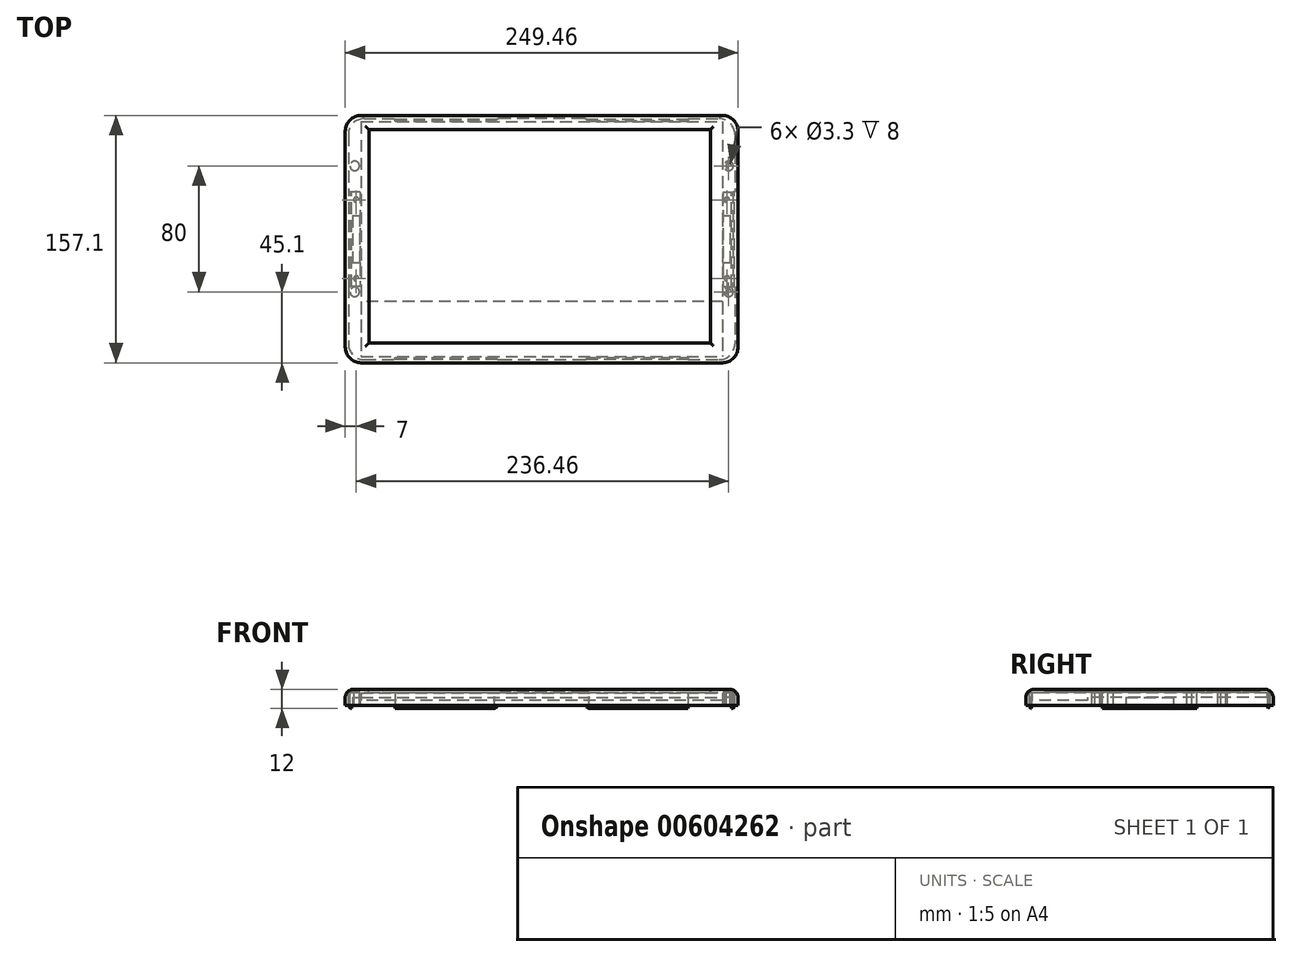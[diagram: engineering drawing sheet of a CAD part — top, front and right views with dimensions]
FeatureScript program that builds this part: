
annotation { "Feature Type Name" : "Feature", "Feature Type Description" : "" }
export const myFeature = defineFeature(function(context is Context, id is Id, definition is map)
    precondition{}
    {
        {
            var Q0;
            Q0=qCreatedBy(makeId("Top.planeOp"),FACE);
            var sketch = newSketch(context, id + "F0", { "sketchPlane" : qUnion([Q0])});
            skLineSegment(sketch, "E0.bottom", {"start": v(-114.73, 74.55) * mm, "end": v(114.73, 74.55) * mm});
            skLineSegment(sketch, "E0.top", {"start": v(-114.73, -74.55) * mm, "end": v(114.73, -74.55) * mm});
            skLineSegment(sketch, "E0.left", {"start": v(-114.73, 74.55) * mm, "end": v(-114.73, -74.55) * mm});
            skLineSegment(sketch, "E0.right", {"start": v(114.73, 74.55) * mm, "end": v(114.73, -74.55) * mm});
            skPoint(sketch, "E0.middle", {"position": v(0, 0) * mm});
            skLineSegment(sketch, "E1.bottom", {"start": v(-111.27, 71.12) * mm, "end": v(108.7, 71.12) * mm});
            skLineSegment(sketch, "E1.top", {"start": v(-111.27, -67.78) * mm, "end": v(108.7, -67.78) * mm});
            skLineSegment(sketch, "E1.left", {"start": v(-111.27, 71.12) * mm, "end": v(-111.27, -67.78) * mm});
            skLineSegment(sketch, "E1.right", {"start": v(108.7, 71.12) * mm, "end": v(108.7, -67.78) * mm});
            skLineSegment(sketch, "E2.bottom", {"start": v(-109.77, 69.62) * mm, "end": v(107.2, 69.62) * mm});
            skLineSegment(sketch, "E2.top", {"start": v(-109.77, -65.98) * mm, "end": v(107.2, -65.98) * mm});
            skLineSegment(sketch, "E2.left", {"start": v(-109.77, 69.62) * mm, "end": v(-109.77, -65.98) * mm});
            skLineSegment(sketch, "E2.right", {"start": v(107.2, 69.62) * mm, "end": v(107.2, -65.98) * mm});
            skLineSegment(sketch, "E3.bottom", {"start": v(-122.73, 76.55) * mm, "end": v(122.73, 76.55) * mm});
            skLineSegment(sketch, "E3.top", {"start": v(-122.73, -76.55) * mm, "end": v(122.73, -76.55) * mm});
            skLineSegment(sketch, "E3.left", {"start": v(-122.73, 76.55) * mm, "end": v(-122.73, -76.55) * mm});
            skLineSegment(sketch, "E3.right", {"start": v(122.73, 76.55) * mm, "end": v(122.73, -76.55) * mm});
            skLineSegment(sketch, "E4.0", {"start": v(-124.73, 78.55) * mm, "end": v(124.73, 78.55) * mm});
            skLineSegment(sketch, "E4.1", {"start": v(-124.73, 78.55) * mm, "end": v(-124.73, -78.55) * mm});
            skLineSegment(sketch, "E4.2", {"start": v(-124.73, -78.55) * mm, "end": v(124.73, -78.55) * mm});
            skLineSegment(sketch, "E4.3", {"start": v(124.73, 78.55) * mm, "end": v(124.73, -78.55) * mm});
            skSolve(sketch);
        }
        {
            var Q0;
            Q0=makeQuery(id+"F0.imprint","IMPRINT",FACE,{"disambiguationData":[TD([[makeQuery(id+"F0.imprint","IMPRINT",EDGE,{"derivedFrom":sQuery(id+"F0.wireOp",EDGE,"E0.bottom")}),-1.0]])]});
            var Q1;
            Q1=makeQuery(id+"F0.imprint","IMPRINT",FACE,{"disambiguationData":[TD([[makeQuery(id+"F0.imprint","IMPRINT",EDGE,{"derivedFrom":sQuery(id+"F0.wireOp",EDGE,"E1.bottom")}),-1.0]])]});
            var Q2;
            Q2=makeQuery(id+"F0.imprint","IMPRINT",FACE,{"disambiguationData":[TD([[makeQuery(id+"F0.imprint","IMPRINT",EDGE,{"derivedFrom":sQuery(id+"F0.wireOp",EDGE,"E0.bottom")}),1.0]])]});
            extrude(context, id + "F1", {"entities" : qUnion([Q0, Q1, Q2]), "depth" : 2 * mm, "offsetDistance" : 25 * mm});
        }
        {
            var Q0;
            Q0=makeQuery(id+"F1.opExtrude","CAP_EDGE",EDGE,{"disambiguationData":[OSD([sQuery(id+"F0.wireOp",EDGE,"E2.left")])],"isStart":false});
            var Q1;
            Q1=makeQuery(id+"F1.opExtrude","CAP_EDGE",EDGE,{"disambiguationData":[OSD([sQuery(id+"F0.wireOp",EDGE,"E2.top")])],"isStart":false});
            var Q2;
            Q2=makeQuery(id+"F1.opExtrude","CAP_EDGE",EDGE,{"disambiguationData":[OSD([sQuery(id+"F0.wireOp",EDGE,"E2.right")])],"isStart":false});
            var Q3;
            Q3=makeQuery(id+"F1.opExtrude","CAP_EDGE",EDGE,{"disambiguationData":[OSD([sQuery(id+"F0.wireOp",EDGE,"E2.bottom")])],"isStart":false});
            fillet(context, id + "F2", {"entities" : qUnion([Q0, Q1, Q2, Q3]), "radius" : 2 * mm, "tangentPropagation" : true, "allowEdgeOverflow" : false});
        }
        {
            var Q0;
            Q0=makeQuery(id+"F0.imprint","IMPRINT",FACE,{"disambiguationData":[TD([[makeQuery(id+"F0.imprint","IMPRINT",EDGE,{"derivedFrom":sQuery(id+"F0.wireOp",EDGE,"E2.bottom")}),-1.0]])]});
            var Q1;
            Q1=makeQuery(id+"F0.imprint","IMPRINT",FACE,{"disambiguationData":[TD([[makeQuery(id+"F0.imprint","IMPRINT",EDGE,{"derivedFrom":sQuery(id+"F0.wireOp",EDGE,"E0.bottom")}),-1.0]])]});
            var Q2;
            Q2=makeQuery(id+"F0.imprint","IMPRINT",FACE,{"disambiguationData":[TD([[makeQuery(id+"F0.imprint","IMPRINT",EDGE,{"derivedFrom":sQuery(id+"F0.wireOp",EDGE,"E1.bottom")}),-1.0]])]});
            extrude(context, id + "F3", {"entities" : qUnion([Q0, Q1, Q2]), "depth" : 4.7 * mm, "offsetDistance" : 25 * mm});
        }
        {
            var Q0;
            Q0=makeQuery(id+"F3.opExtrude","SWEPT_BODY",BODY,{"disambiguationData":[OSD([sQuery(id+"F0.wireOp",EDGE,"E0.bottom"),sQuery(id+"F0.wireOp",EDGE,"E0.top"),sQuery(id+"F0.wireOp",EDGE,"E0.left"),sQuery(id+"F0.wireOp",EDGE,"E0.right")])]});
            transform(context, id + "F4", {"entities" : qUnion([Q0]), "transformType" : TransformType.TRANSLATION_3D, "dx" : 0 * mm, "dy" : 0 * mm, "dz" : -4.8 * mm, "makeCopy" : false});
        }
        {
            var Q0;
            Q0=makeQuery(id+"F3.opExtrude","CAP_FACE",FACE,{"disambiguationData":[OSD([sQuery(id+"F0.wireOp",EDGE,"E0.bottom"),sQuery(id+"F0.wireOp",EDGE,"E0.top"),sQuery(id+"F0.wireOp",EDGE,"E0.left"),sQuery(id+"F0.wireOp",EDGE,"E0.right")])],"isStart":true});
            var sketch = newSketch(context, id + "F5", { "sketchPlane" : qUnion([Q0])});
            skLineSegment(sketch, "E5", {"start": v(114.73, 39.55) * mm, "end": v(-114.73, 39.55) * mm});
            skSolve(sketch);
        }
        {
            var Q0;
            Q0=qSketchRegion(id+"F5",true);
            var Q1;
            {var subQ0=sQuery(id+"F5.wireOp",EDGE,"E5");Q1=makeQuery(id+"F5.imprint","IMPRINT",FACE,{"disambiguationData":[TD([[makeQuery(id+"F5.imprint","IMPRINT",EDGE,{"derivedFrom":subQ0}),1.0]])]});}
            extrude(context, id + "F6", {"entities" : qUnion([Q0, Q1]), "operationType" : NewBodyOperationType.REMOVE, "oppositeDirection" : true, "depth" : 1.75 * mm, "offsetDistance" : 25 * mm});
        }
        {
            var Q0;
            Q0=makeQuery(id+"F1.opExtrude","CAP_FACE",FACE,{"disambiguationData":[OSD([sQuery(id+"F0.wireOp",EDGE,"E2.bottom"),sQuery(id+"F0.wireOp",EDGE,"E2.top"),sQuery(id+"F0.wireOp",EDGE,"E2.left"),sQuery(id+"F0.wireOp",EDGE,"E2.right"),sQuery(id+"F0.wireOp",EDGE,"E3.bottom"),sQuery(id+"F0.wireOp",EDGE,"E3.top"),sQuery(id+"F0.wireOp",EDGE,"E3.left"),sQuery(id+"F0.wireOp",EDGE,"E3.right")])],"isStart":true});
            var sketch = newSketch(context, id + "F7", { "sketchPlane" : qUnion([Q0])});
            skCircle(sketch, "E6", {"center": v(118.73, -46.55) * mm, "radius": 3 * mm});
            skCircle(sketch, "E7", {"center": v(118.73, 33.45) * mm, "radius": 3 * mm});
            skCircle(sketch, "E8.MirrorC", {"center": v(-118.73, -46.55) * mm, "radius": 3 * mm});
            skCircle(sketch, "E9.MirrorC", {"center": v(-118.73, 33.45) * mm, "radius": 3 * mm});
            skSolve(sketch);
        }
        {
            var Q0;
            Q0=qSketchRegion(id+"F7",true);
            extrude(context, id + "F8", {"entities" : qUnion([Q0]), "operationType" : NewBodyOperationType.ADD, "depth" : 8 * mm, "offsetDistance" : 25 * mm});
        }
        {
            var Q0;
            Q0=makeQuery(id+"F0.imprint","IMPRINT",FACE,{"disambiguationData":[TD([[makeQuery(id+"F0.imprint","IMPRINT",EDGE,{"derivedFrom":sQuery(id+"F0.wireOp",EDGE,"E3.bottom")}),1.0]])]});
            var Q1;
            Q1=makeQuery(id+"F1.opExtrude","CAP_FACE",FACE,{"disambiguationData":[OSD([sQuery(id+"F0.wireOp",EDGE,"E2.bottom"),sQuery(id+"F0.wireOp",EDGE,"E2.top"),sQuery(id+"F0.wireOp",EDGE,"E2.left"),sQuery(id+"F0.wireOp",EDGE,"E2.right"),sQuery(id+"F0.wireOp",EDGE,"E3.bottom"),sQuery(id+"F0.wireOp",EDGE,"E3.top"),sQuery(id+"F0.wireOp",EDGE,"E3.left"),sQuery(id+"F0.wireOp",EDGE,"E3.right")])],"isStart":false});
            extrude(context, id + "F9", {"entities" : qUnion([Q0]), "operationType" : NewBodyOperationType.ADD, "endBound" : BoundingType.UP_TO_SURFACE, "depth" : 25 * mm, "endBoundEntityFace" : qUnion([Q1]), "offsetDistance" : 25 * mm});
        }
        {
            var Q0;
            Q0=makeQuery(id+"F0.imprint","IMPRINT",FACE,{"disambiguationData":[TD([[makeQuery(id+"F0.imprint","IMPRINT",EDGE,{"derivedFrom":sQuery(id+"F0.wireOp",EDGE,"E3.bottom")}),1.0]])]});
            extrude(context, id + "F10", {"entities" : qUnion([Q0]), "operationType" : NewBodyOperationType.ADD, "oppositeDirection" : true, "depth" : 8 * mm, "offsetDistance" : 25 * mm});
        }
        {
            var Q0;
            Q0=makeQuery(id+"F10.opExtrude","SWEPT_FACE",FACE,{"disambiguationData":[OSD([sQuery(id+"F0.wireOp",EDGE,"E3.top")])]});
            var sketch = newSketch(context, id + "F11", { "sketchPlane" : qUnion([Q0])});
            skLineSegment(sketch, "E10.bottom", {"start": v(-93, 0) * mm, "end": v(-85, 0) * mm});
            skLineSegment(sketch, "E10.top", {"start": v(-93, -8) * mm, "end": v(-85, -8) * mm});
            skLineSegment(sketch, "E10.left", {"start": v(-93, 0) * mm, "end": v(-93, -8) * mm});
            skLineSegment(sketch, "E10.right", {"start": v(-85, 0) * mm, "end": v(-85, -8) * mm});
            skLineSegment(sketch, "E11.MirrorCS", {"start": v(93, 0) * mm, "end": v(93, -8) * mm});
            skLineSegment(sketch, "E12.MirrorCS", {"start": v(93, 0) * mm, "end": v(85, 0) * mm});
            skLineSegment(sketch, "E13.MirrorCS", {"start": v(85, 0) * mm, "end": v(85, -8) * mm});
            skLineSegment(sketch, "E14.MirrorCS", {"start": v(93, -8) * mm, "end": v(85, -8) * mm});
            skSolve(sketch);
        }
        {
            var Q0;
            Q0=makeQuery(id+"F11.imprint","IMPRINT",FACE,{"disambiguationData":[TD([[makeQuery(id+"F11.imprint","IMPRINT",EDGE,{"derivedFrom":sQuery(id+"F11.wireOp",EDGE,"E10.bottom")}),1.0]])]});
            var Q1;
            Q1=makeQuery(id+"F11.imprint","IMPRINT",FACE,{"disambiguationData":[TD([[makeQuery(id+"F11.imprint","IMPRINT",EDGE,{"derivedFrom":sQuery(id+"F11.wireOp",EDGE,"E11.MirrorCS")}),-1.0]])]});
            extrude(context, id + "F12", {"entities" : qUnion([Q0, Q1]), "operationType" : NewBodyOperationType.ADD, "depth" : 1.7 * mm, "offsetDistance" : 25 * mm});
        }
        {
            var Q0;
            Q0=makeQuery(id+"F10.opExtrude","SWEPT_FACE",FACE,{"disambiguationData":[OSD([sQuery(id+"F0.wireOp",EDGE,"E3.bottom")])]});
            var sketch = newSketch(context, id + "F13", { "sketchPlane" : qUnion([Q0])});
            skLineSegment(sketch, "E15.bottom", {"start": v(-93, 0) * mm, "end": v(-85, 0) * mm});
            skLineSegment(sketch, "E15.top", {"start": v(-93, -8) * mm, "end": v(-85, -8) * mm});
            skLineSegment(sketch, "E15.left", {"start": v(-93, 0) * mm, "end": v(-93, -8) * mm});
            skLineSegment(sketch, "E15.right", {"start": v(-85, 0) * mm, "end": v(-85, -8) * mm});
            skLineSegment(sketch, "E16.MirrorCS", {"start": v(93, 0) * mm, "end": v(93, -8) * mm});
            skLineSegment(sketch, "E17.MirrorCS", {"start": v(85, 0) * mm, "end": v(85, -8) * mm});
            skLineSegment(sketch, "E18.MirrorCS", {"start": v(93, 0) * mm, "end": v(85, 0) * mm});
            skLineSegment(sketch, "E19.MirrorCS", {"start": v(93, -8) * mm, "end": v(85, -8) * mm});
            skSolve(sketch);
        }
        {
            var Q0;
            Q0=makeQuery(id+"F13.imprint","IMPRINT",FACE,{"disambiguationData":[TD([[makeQuery(id+"F13.imprint","IMPRINT",EDGE,{"derivedFrom":sQuery(id+"F13.wireOp",EDGE,"E15.bottom")}),-1.0]])]});
            var Q1;
            Q1=makeQuery(id+"F13.imprint","IMPRINT",FACE,{"disambiguationData":[TD([[makeQuery(id+"F13.imprint","IMPRINT",EDGE,{"derivedFrom":sQuery(id+"F13.wireOp",EDGE,"E16.MirrorCS")}),-1.0]])]});
            extrude(context, id + "F14", {"entities" : qUnion([Q0, Q1]), "operationType" : NewBodyOperationType.ADD, "depth" : 1.7 * mm, "offsetDistance" : 25 * mm});
        }
        {
            var Q0;
            Q0=makeQuery(id+"F10.opExtrude","SWEPT_FACE",FACE,{"disambiguationData":[OSD([sQuery(id+"F0.wireOp",EDGE,"E3.left")])]});
            var sketch = newSketch(context, id + "F15", { "sketchPlane" : qUnion([Q0])});
            skLineSegment(sketch, "E20.bottom", {"start": v(-30, -8) * mm, "end": v(30, -8) * mm});
            skLineSegment(sketch, "E20.top", {"start": v(-30, 0) * mm, "end": v(30, 0) * mm});
            skLineSegment(sketch, "E20.left", {"start": v(-30, -8) * mm, "end": v(-30, 0) * mm});
            skLineSegment(sketch, "E20.right", {"start": v(30, -8) * mm, "end": v(30, 0) * mm});
            skSolve(sketch);
        }
        {
            var Q0;
            Q0=makeQuery(id+"F15.imprint","IMPRINT",FACE,{"disambiguationData":[TD([[makeQuery(id+"F15.imprint","IMPRINT",EDGE,{"derivedFrom":sQuery(id+"F15.wireOp",EDGE,"E20.bottom")}),-1.0]])]});
            extrude(context, id + "F16", {"entities" : qUnion([Q0]), "depth" : 7.7 * mm, "offsetDistance" : 25 * mm});
        }
        {
            var Q0;
            Q0=makeQuery(id+"F16.opExtrude","SWEPT_BODY",BODY,{"disambiguationData":[OSD([sQuery(id+"F15.wireOp",EDGE,"E20.bottom"),sQuery(id+"F15.wireOp",EDGE,"E20.top"),sQuery(id+"F15.wireOp",EDGE,"E20.left"),sQuery(id+"F15.wireOp",EDGE,"E20.right")])]});
            var Q1;
            Q1=qCreatedBy(makeId("Right.planeOp"),FACE);
            mirror(context, id + "F17", {"operationType" : NewBodyOperationType.ADD, "entities" : qUnion([Q0]), "mirrorPlane" : qUnion([Q1])});
        }
        {
            var Q0;
            {var subQ0=makeQuery(id+"F16.opExtrude","SWEPT_FACE",FACE,{"disambiguationData":[OSD([sQuery(id+"F15.wireOp",EDGE,"E20.bottom")])]});Q0=makeQuery(id+"F17.boolean.opBoolean","MERGE",FACE,{"derivedFrom":[makeQuery(id+"F14.boolean.opBoolean","MERGE",FACE,{"derivedFrom":[makeQuery(id+"F12.boolean.opBoolean","MERGE",FACE,{"derivedFrom":[makeQuery(id+"F10.opExtrude","CAP_FACE",FACE,{"disambiguationData":[OSD([sQuery(id+"F0.wireOp",EDGE,"E3.bottom"),sQuery(id+"F0.wireOp",EDGE,"E3.top"),sQuery(id+"F0.wireOp",EDGE,"E3.left"),sQuery(id+"F0.wireOp",EDGE,"E3.right"),sQuery(id+"F0.wireOp",EDGE,"E4.0"),sQuery(id+"F0.wireOp",EDGE,"E4.1"),sQuery(id+"F0.wireOp",EDGE,"E4.2"),sQuery(id+"F0.wireOp",EDGE,"E4.3")])],"isStart":false}),makeQuery(id+"F12.opExtrude","SWEPT_FACE",FACE,{"disambiguationData":[OSD([sQuery(id+"F11.wireOp",EDGE,"E10.top")])]}),makeQuery(id+"F12.opExtrude","SWEPT_FACE",FACE,{"disambiguationData":[OSD([sQuery(id+"F11.wireOp",EDGE,"E14.MirrorCS")])]})]}),makeQuery(id+"F14.opExtrude","SWEPT_FACE",FACE,{"disambiguationData":[OSD([sQuery(id+"F13.wireOp",EDGE,"E15.top")])]}),makeQuery(id+"F14.opExtrude","SWEPT_FACE",FACE,{"disambiguationData":[OSD([sQuery(id+"F13.wireOp",EDGE,"E19.MirrorCS")])]})]}),subQ0,makeQuery(id+"F17.opPattern","COPY",FACE,{"derivedFrom":subQ0,"instanceName":"1"})]});}
            var sketch = newSketch(context, id + "F18", { "sketchPlane" : qUnion([Q0])});
            skLineSegment(sketch, "E21.bottom", {"start": v(-115.03, 15) * mm, "end": v(-120.03, 15) * mm});
            skLineSegment(sketch, "E21.top", {"start": v(-115.03, -15) * mm, "end": v(-120.03, -15) * mm});
            skLineSegment(sketch, "E21.left", {"start": v(-115.03, 15) * mm, "end": v(-115.03, -15) * mm});
            skLineSegment(sketch, "E21.right", {"start": v(-120.03, 15) * mm, "end": v(-120.03, -15) * mm});
            skLineSegment(sketch, "E22.MirrorCS", {"start": v(115.03, 15) * mm, "end": v(120.03, 15) * mm});
            skLineSegment(sketch, "E23.MirrorCS", {"start": v(115.03, -15) * mm, "end": v(120.03, -15) * mm});
            skLineSegment(sketch, "E24.MirrorCS", {"start": v(115.03, 15) * mm, "end": v(115.03, -15) * mm});
            skLineSegment(sketch, "E25.MirrorCS", {"start": v(120.03, 15) * mm, "end": v(120.03, -15) * mm});
            skSolve(sketch);
        }
        {
            var Q0;
            Q0=qSketchRegion(id+"F18",true);
            var Q1;
            Q1=makeQuery(id+"F6.boolean.opBoolean","COPY",FACE,{"derivedFrom":makeQuery(id+"F6.opExtrude","CAP_FACE",FACE,{"disambiguationData":[OSD([sQuery(id+"F0.wireOp",EDGE,"E0.bottom"),sQuery(id+"F0.wireOp",EDGE,"E0.left"),sQuery(id+"F0.wireOp",EDGE,"E0.right"),sQuery(id+"F5.wireOp",EDGE,"E5")])],"isStart":false})});
            extrude(context, id + "F19", {"entities" : qUnion([Q0]), "operationType" : NewBodyOperationType.REMOVE, "endBound" : BoundingType.UP_TO_SURFACE, "oppositeDirection" : true, "depth" : 25 * mm, "endBoundEntityFace" : qUnion([Q1]), "offsetDistance" : 25 * mm});
        }
        {
            var Q0;
            {var subQ0=makeQuery(id+"F16.opExtrude","SWEPT_FACE",FACE,{"disambiguationData":[OSD([sQuery(id+"F15.wireOp",EDGE,"E20.bottom")])]});Q0=makeQuery(id+"F17.boolean.opBoolean","MERGE",FACE,{"derivedFrom":[makeQuery(id+"F14.boolean.opBoolean","MERGE",FACE,{"derivedFrom":[makeQuery(id+"F12.boolean.opBoolean","MERGE",FACE,{"derivedFrom":[makeQuery(id+"F10.opExtrude","CAP_FACE",FACE,{"disambiguationData":[OSD([sQuery(id+"F0.wireOp",EDGE,"E3.bottom"),sQuery(id+"F0.wireOp",EDGE,"E3.top"),sQuery(id+"F0.wireOp",EDGE,"E3.left"),sQuery(id+"F0.wireOp",EDGE,"E3.right"),sQuery(id+"F0.wireOp",EDGE,"E4.0"),sQuery(id+"F0.wireOp",EDGE,"E4.1"),sQuery(id+"F0.wireOp",EDGE,"E4.2"),sQuery(id+"F0.wireOp",EDGE,"E4.3")])],"isStart":false}),makeQuery(id+"F12.opExtrude","SWEPT_FACE",FACE,{"disambiguationData":[OSD([sQuery(id+"F11.wireOp",EDGE,"E10.top")])]}),makeQuery(id+"F12.opExtrude","SWEPT_FACE",FACE,{"disambiguationData":[OSD([sQuery(id+"F11.wireOp",EDGE,"E14.MirrorCS")])]})]}),makeQuery(id+"F14.opExtrude","SWEPT_FACE",FACE,{"disambiguationData":[OSD([sQuery(id+"F13.wireOp",EDGE,"E15.top")])]}),makeQuery(id+"F14.opExtrude","SWEPT_FACE",FACE,{"disambiguationData":[OSD([sQuery(id+"F13.wireOp",EDGE,"E19.MirrorCS")])]})]}),subQ0,makeQuery(id+"F17.opPattern","COPY",FACE,{"derivedFrom":subQ0,"instanceName":"1"})]});}
            var sketch = newSketch(context, id + "F20", { "sketchPlane" : qUnion([Q0])});
            skCircle(sketch, "E26", {"center": v(-117.73, 25) * mm, "radius": 1.65 * mm});
            skCircle(sketch, "E27.MirrorC", {"center": v(-117.73, -25) * mm, "radius": 1.65 * mm});
            skCircle(sketch, "E28.MirrorC", {"center": v(117.73, 25) * mm, "radius": 1.65 * mm});
            skCircle(sketch, "E29.MirrorC", {"center": v(117.73, -25) * mm, "radius": 1.65 * mm});
            skSolve(sketch);
        }
        {
            var Q0;
            Q0=qSketchRegion(id+"F20",true);
            extrude(context, id + "F21", {"entities" : qUnion([Q0]), "operationType" : NewBodyOperationType.REMOVE, "oppositeDirection" : true, "depth" : 8 * mm, "offsetDistance" : 25 * mm});
        }
        {
            var Q0;
            {var subQ0=makeQuery(id+"F16.opExtrude","SWEPT_FACE",FACE,{"disambiguationData":[OSD([sQuery(id+"F15.wireOp",EDGE,"E20.bottom")])]});Q0=makeQuery(id+"F17.boolean.opBoolean","MERGE",FACE,{"derivedFrom":[makeQuery(id+"F14.boolean.opBoolean","MERGE",FACE,{"derivedFrom":[makeQuery(id+"F12.boolean.opBoolean","MERGE",FACE,{"derivedFrom":[makeQuery(id+"F10.opExtrude","CAP_FACE",FACE,{"disambiguationData":[OSD([sQuery(id+"F0.wireOp",EDGE,"E3.bottom"),sQuery(id+"F0.wireOp",EDGE,"E3.top"),sQuery(id+"F0.wireOp",EDGE,"E3.left"),sQuery(id+"F0.wireOp",EDGE,"E3.right"),sQuery(id+"F0.wireOp",EDGE,"E4.0"),sQuery(id+"F0.wireOp",EDGE,"E4.1"),sQuery(id+"F0.wireOp",EDGE,"E4.2"),sQuery(id+"F0.wireOp",EDGE,"E4.3")])],"isStart":false}),makeQuery(id+"F12.opExtrude","SWEPT_FACE",FACE,{"disambiguationData":[OSD([sQuery(id+"F11.wireOp",EDGE,"E10.top")])]}),makeQuery(id+"F12.opExtrude","SWEPT_FACE",FACE,{"disambiguationData":[OSD([sQuery(id+"F11.wireOp",EDGE,"E14.MirrorCS")])]})]}),makeQuery(id+"F14.opExtrude","SWEPT_FACE",FACE,{"disambiguationData":[OSD([sQuery(id+"F13.wireOp",EDGE,"E15.top")])]}),makeQuery(id+"F14.opExtrude","SWEPT_FACE",FACE,{"disambiguationData":[OSD([sQuery(id+"F13.wireOp",EDGE,"E19.MirrorCS")])]})]}),subQ0,makeQuery(id+"F17.opPattern","COPY",FACE,{"derivedFrom":subQ0,"instanceName":"1"})]});}
            var sketch = newSketch(context, id + "F22", { "sketchPlane" : qUnion([Q0])});
            skLineSegment(sketch, "E30.bottom", {"start": v(-122.73, 30) * mm, "end": v(-120.73, 30) * mm});
            skLineSegment(sketch, "E30.top", {"start": v(-122.73, -30) * mm, "end": v(-120.73, -30) * mm});
            skLineSegment(sketch, "E30.left", {"start": v(-122.73, 30) * mm, "end": v(-122.73, -30) * mm});
            skLineSegment(sketch, "E30.right", {"start": v(-120.73, 30) * mm, "end": v(-120.73, -30) * mm});
            skLineSegment(sketch, "E31", {"start": v(-122.43, 30) * mm, "end": v(-122.43, -30) * mm});
            skSolve(sketch);
        }
        {
            var Q0;
            {var subQ0=sQuery(id+"F22.wireOp",EDGE,"E30.right");Q0=makeQuery(id+"F22.imprint","IMPRINT",FACE,{"disambiguationData":[TD([[makeQuery(id+"F22.imprint","IMPRINT",EDGE,{"derivedFrom":subQ0}),-1.0]])]});}
            extrude(context, id + "F23", {"entities" : qUnion([Q0]), "depth" : 2 * mm, "offsetDistance" : 25 * mm});
        }
        {
            var Q0;
            Q0=makeQuery(id+"F23.opExtrude","SWEPT_BODY",BODY,{"disambiguationData":[OSD([sQuery(id+"F22.wireOp",EDGE,"E30.bottom"),sQuery(id+"F22.wireOp",EDGE,"E30.top"),sQuery(id+"F22.wireOp",EDGE,"E30.left"),sQuery(id+"F22.wireOp",EDGE,"E30.right")])]});
            var Q1;
            Q1=qCreatedBy(makeId("Right.planeOp"),FACE);
            mirror(context, id + "F24", {"operationType" : NewBodyOperationType.ADD, "entities" : qUnion([Q0]), "mirrorPlane" : qUnion([Q1])});
        }
        {
            var Q0;
            Q0=makeQuery(id+"F23.opExtrude","CAP_EDGE",EDGE,{"disambiguationData":[OSD([sQuery(id+"F22.wireOp",EDGE,"E31")])],"isStart":false});
            var Q1;
            Q1=makeQuery(id+"F24.opPattern","COPY",EDGE,{"derivedFrom":makeQuery(id+"F23.opExtrude","CAP_EDGE",EDGE,{"disambiguationData":[OSD([sQuery(id+"F22.wireOp",EDGE,"E31")])],"isStart":false}),"instanceName":"1"});
            chamfer(context, id + "F25", {"entities" : qUnion([Q0, Q1]), "width" : 1 * mm, "tangentPropagation" : true});
        }
        {
            var Q0;
            {var subQ0=sQuery(id+"F11.wireOp",EDGE,"E14.MirrorCS");var subQ5=sQuery(id+"F13.wireOp",EDGE,"E15.top");var subQ9=sQuery(id+"F11.wireOp",EDGE,"E10.top");var subQ10=sQuery(id+"F0.wireOp",EDGE,"E4.2");var subQ12=sQuery(id+"F0.wireOp",EDGE,"E4.3");var subQ14=sQuery(id+"F0.wireOp",EDGE,"E4.0");var subQ15=sQuery(id+"F0.wireOp",EDGE,"E3.right");var subQ16=sQuery(id+"F0.wireOp",EDGE,"E3.bottom");var subQ18=sQuery(id+"F0.wireOp",EDGE,"E4.1");var subQ19=sQuery(id+"F0.wireOp",EDGE,"E3.left");var subQ20=sQuery(id+"F0.wireOp",EDGE,"E3.top");var subQ21=sQuery(id+"F13.wireOp",EDGE,"E19.MirrorCS");var subQ25=makeQuery(id+"F16.opExtrude","SWEPT_FACE",FACE,{"disambiguationData":[OSD([sQuery(id+"F15.wireOp",EDGE,"E20.bottom")])]});Q0=makeQuery(id+"F24.boolean.opBoolean","SPLIT",FACE,{"disambiguationData":[TD([makeQuery(id+"F9.opExtrude","SWEPT_FACE",FACE,{"disambiguationData":[OSD([subQ14])]})])],"derivedFrom":makeQuery(id+"F17.boolean.opBoolean","MERGE",FACE,{"derivedFrom":[makeQuery(id+"F14.boolean.opBoolean","MERGE",FACE,{"derivedFrom":[makeQuery(id+"F12.boolean.opBoolean","MERGE",FACE,{"derivedFrom":[makeQuery(id+"F10.opExtrude","CAP_FACE",FACE,{"disambiguationData":[OSD([subQ16,subQ20,subQ19,subQ15,subQ14,subQ18,subQ10,subQ12])],"isStart":false}),makeQuery(id+"F12.opExtrude","SWEPT_FACE",FACE,{"disambiguationData":[OSD([subQ9])]}),makeQuery(id+"F12.opExtrude","SWEPT_FACE",FACE,{"disambiguationData":[OSD([subQ0])]})]}),makeQuery(id+"F14.opExtrude","SWEPT_FACE",FACE,{"disambiguationData":[OSD([subQ5])]}),makeQuery(id+"F14.opExtrude","SWEPT_FACE",FACE,{"disambiguationData":[OSD([subQ21])]})]}),subQ25,makeQuery(id+"F17.opPattern","COPY",FACE,{"derivedFrom":subQ25,"instanceName":"1"})]})});}
            var sketch = newSketch(context, id + "F26", { "sketchPlane" : qUnion([Q0])});
            skLineSegment(sketch, "E32.bottom", {"start": v(-93, -74.85) * mm, "end": v(-85, -74.85) * mm});
            skLineSegment(sketch, "E32.top", {"start": v(-93, -76.55) * mm, "end": v(-85, -76.55) * mm});
            skLineSegment(sketch, "E32.left", {"start": v(-93, -74.85) * mm, "end": v(-93, -76.55) * mm});
            skLineSegment(sketch, "E32.right", {"start": v(-85, -74.85) * mm, "end": v(-85, -76.55) * mm});
            skLineSegment(sketch, "E33.top", {"start": v(-93, -76.25) * mm, "end": v(-85, -76.25) * mm});
            skLineSegment(sketch, "E33.left", {"start": v(-93, -76.55) * mm, "end": v(-93, -76.25) * mm});
            skLineSegment(sketch, "E33.right", {"start": v(-85, -76.55) * mm, "end": v(-85, -76.25) * mm});
            skSolve(sketch);
        }
        {
            var Q0;
            {var subQ0=sQuery(id+"F26.wireOp",EDGE,"E32.bottom");Q0=makeQuery(id+"F26.imprint","IMPRINT",FACE,{"disambiguationData":[TD([[makeQuery(id+"F26.imprint","IMPRINT",EDGE,{"derivedFrom":subQ0}),-1.0]])]});}
            var Q1;
            Q1=makeQuery(id+"F23.opExtrude","CAP_FACE",FACE,{"disambiguationData":[OSD([sQuery(id+"F22.wireOp",EDGE,"E30.bottom"),sQuery(id+"F22.wireOp",EDGE,"E30.top"),sQuery(id+"F22.wireOp",EDGE,"E30.right"),sQuery(id+"F22.wireOp",EDGE,"E31")])],"isStart":false});
            extrude(context, id + "F27", {"entities" : qUnion([Q0]), "endBound" : BoundingType.UP_TO_SURFACE, "depth" : 25 * mm, "endBoundEntityFace" : qUnion([Q1]), "offsetDistance" : 25 * mm});
        }
        {
            var Q0;
            Q0=makeQuery(id+"F27.opExtrude","CAP_EDGE",EDGE,{"disambiguationData":[OSD([sQuery(id+"F26.wireOp",EDGE,"E33.top")])],"isStart":false});
            chamfer(context, id + "F28", {"entities" : qUnion([Q0]), "width" : 1 * mm, "tangentPropagation" : true});
        }
        {
            var Q0;
            Q0=makeQuery(id+"F27.opExtrude","SWEPT_BODY",BODY,{"disambiguationData":[OSD([sQuery(id+"F26.wireOp",EDGE,"E32.bottom"),sQuery(id+"F26.wireOp",EDGE,"E32.left"),sQuery(id+"F26.wireOp",EDGE,"E32.right"),sQuery(id+"F26.wireOp",EDGE,"E33.top")])]});
            var Q1;
            Q1=qCreatedBy(makeId("Right.planeOp"),FACE);
            mirror(context, id + "F29", {"entities" : qUnion([Q0]), "mirrorPlane" : qUnion([Q1])});
        }
        {
            var Q0;
            Q0=makeQuery(id+"F27.opExtrude","SWEPT_BODY",BODY,{"disambiguationData":[OSD([sQuery(id+"F26.wireOp",EDGE,"E32.bottom"),sQuery(id+"F26.wireOp",EDGE,"E32.left"),sQuery(id+"F26.wireOp",EDGE,"E32.right"),sQuery(id+"F26.wireOp",EDGE,"E33.top")])]});
            var Q1;
            Q1=makeQuery(id+"F29.opPattern","COPY",BODY,{"derivedFrom":makeQuery(id+"F27.opExtrude","SWEPT_BODY",BODY,{"disambiguationData":[OSD([sQuery(id+"F26.wireOp",EDGE,"E32.bottom"),sQuery(id+"F26.wireOp",EDGE,"E32.left"),sQuery(id+"F26.wireOp",EDGE,"E32.right"),sQuery(id+"F26.wireOp",EDGE,"E33.top")])]}),"instanceName":"1"});
            var Q2;
            Q2=qCreatedBy(makeId("Front.planeOp"),FACE);
            mirror(context, id + "F30", {"operationType" : NewBodyOperationType.ADD, "entities" : qUnion([Q0, Q1]), "mirrorPlane" : qUnion([Q2])});
        }
        {
            var Q0;
            Q0=makeQuery(id+"F8.opExtrude","CAP_FACE",FACE,{"disambiguationData":[OSD([sQuery(id+"F7.wireOp",EDGE,"E6")])],"isStart":false});
            var sketch = newSketch(context, id + "F31", { "sketchPlane" : qUnion([Q0])});
            skCircle(sketch, "E34", {"center": v(118.73, -46.55) * mm, "radius": 1.65 * mm});
            skCircle(sketch, "E35.MirrorC", {"center": v(-118.73, -46.55) * mm, "radius": 1.65 * mm});
            skSolve(sketch);
        }
        {
            var Q0;
            Q0=makeQuery(id+"F8.opExtrude","CAP_FACE",FACE,{"disambiguationData":[OSD([sQuery(id+"F7.wireOp",EDGE,"E7")])],"isStart":false});
            var sketch = newSketch(context, id + "F32", { "sketchPlane" : qUnion([Q0])});
            skCircle(sketch, "E36", {"center": v(118.73, 33.45) * mm, "radius": 1.65 * mm});
            skCircle(sketch, "E37.MirrorC", {"center": v(-118.73, 33.45) * mm, "radius": 1.65 * mm});
            skSolve(sketch);
        }
        {
            var Q0;
            Q0=makeQuery(id+"F31.imprint","IMPRINT",FACE,{"disambiguationData":[TD([[makeQuery(id+"F31.imprint","IMPRINT",EDGE,{"derivedFrom":sQuery(id+"F31.wireOp",EDGE,"E34")}),1.0]])]});
            var Q1;
            Q1=makeQuery(id+"F31.imprint","IMPRINT",FACE,{"disambiguationData":[TD([[makeQuery(id+"F31.imprint","IMPRINT",EDGE,{"derivedFrom":sQuery(id+"F31.wireOp",EDGE,"E35.MirrorC")}),-1.0]])]});
            var Q2;
            Q2=makeQuery(id+"F32.imprint","IMPRINT",FACE,{"disambiguationData":[TD([[makeQuery(id+"F32.imprint","IMPRINT",EDGE,{"derivedFrom":sQuery(id+"F32.wireOp",EDGE,"E37.MirrorC")}),-1.0]])]});
            var Q3;
            Q3=makeQuery(id+"F32.imprint","IMPRINT",FACE,{"disambiguationData":[TD([[makeQuery(id+"F32.imprint","IMPRINT",EDGE,{"derivedFrom":sQuery(id+"F32.wireOp",EDGE,"E36")}),1.0]])]});
            extrude(context, id + "F33", {"entities" : qUnion([Q0, Q1, Q2, Q3]), "operationType" : NewBodyOperationType.REMOVE, "oppositeDirection" : true, "depth" : 8 * mm, "offsetDistance" : 25 * mm});
        }
        {
            var Q0;
            Q0=makeQuery(id+"F30.boolean.opBoolean","MERGE",FACE,{"derivedFrom":[makeQuery(id+"F14.opExtrude","SWEPT_FACE",FACE,{"disambiguationData":[OSD([sQuery(id+"F13.wireOp",EDGE,"E17.MirrorCS")])]}),makeQuery(id+"F29.opPattern","COPY",FACE,{"derivedFrom":makeQuery(id+"F27.opExtrude","SWEPT_FACE",FACE,{"disambiguationData":[OSD([sQuery(id+"F26.wireOp",EDGE,"E32.right")])]}),"instanceName":"1"})]});
            var Q1;
            Q1=makeQuery(id+"F30.boolean.opBoolean","MERGE",FACE,{"derivedFrom":[makeQuery(id+"F12.opExtrude","SWEPT_FACE",FACE,{"disambiguationData":[OSD([sQuery(id+"F11.wireOp",EDGE,"E10.right")])]}),makeQuery(id+"F30.opPattern","COPY",FACE,{"derivedFrom":makeQuery(id+"F29.opPattern","COPY",FACE,{"derivedFrom":makeQuery(id+"F27.opExtrude","SWEPT_FACE",FACE,{"disambiguationData":[OSD([sQuery(id+"F26.wireOp",EDGE,"E32.right")])]}),"instanceName":"1"}),"instanceName":"1"})]});
            extrude(context, id + "F34", {"entities" : qUnion([Q0, Q1]), "operationType" : NewBodyOperationType.ADD, "endBound" : BoundingType.UP_TO_NEXT, "depth" : 25 * mm, "offsetDistance" : 25 * mm});
        }
        {
            var Q0;
            Q0=makeQuery(id+"F10.opExtrude","SWEPT_EDGE",EDGE,{"disambiguationData":[OSD([sQuery(id+"F0.wireOp",EDGE,"E3.bottom"),sQuery(id+"F0.wireOp",EDGE,"E3.left")])]});
            var Q1;
            Q1=makeQuery(id+"F10.opExtrude","SWEPT_EDGE",EDGE,{"disambiguationData":[OSD([sQuery(id+"F0.wireOp",EDGE,"E3.bottom"),sQuery(id+"F0.wireOp",EDGE,"E3.right")])]});
            var Q2;
            Q2=makeQuery(id+"F10.opExtrude","SWEPT_EDGE",EDGE,{"disambiguationData":[OSD([sQuery(id+"F0.wireOp",EDGE,"E3.top"),sQuery(id+"F0.wireOp",EDGE,"E3.left")])]});
            var Q3;
            Q3=makeQuery(id+"F10.opExtrude","SWEPT_EDGE",EDGE,{"disambiguationData":[OSD([sQuery(id+"F0.wireOp",EDGE,"E3.top"),sQuery(id+"F0.wireOp",EDGE,"E3.right")])]});
            fillet(context, id + "F35", {"entities" : qUnion([Q0, Q1, Q2, Q3]), "radius" : 10 * mm, "tangentPropagation" : true, "allowEdgeOverflow" : false});
        }
        {
            var Q0;
            {var subQ0=sQuery(id+"F0.wireOp",EDGE,"E4.1");var subQ1=sQuery(id+"F0.wireOp",EDGE,"E4.0");Q0=makeQuery(id+"F10.boolean.opBoolean","MERGE",EDGE,{"derivedFrom":[makeQuery(id+"F9.opExtrude","SWEPT_EDGE",EDGE,{"disambiguationData":[OSD([subQ1,subQ0])]}),makeQuery(id+"F10.opExtrude","SWEPT_EDGE",EDGE,{"disambiguationData":[OSD([subQ1,subQ0])]})]});}
            var Q1;
            {var subQ0=sQuery(id+"F0.wireOp",EDGE,"E4.2");var subQ1=sQuery(id+"F0.wireOp",EDGE,"E4.1");Q1=makeQuery(id+"F10.boolean.opBoolean","MERGE",EDGE,{"derivedFrom":[makeQuery(id+"F9.opExtrude","SWEPT_EDGE",EDGE,{"disambiguationData":[OSD([subQ1,subQ0])]}),makeQuery(id+"F10.opExtrude","SWEPT_EDGE",EDGE,{"disambiguationData":[OSD([subQ1,subQ0])]})]});}
            var Q2;
            {var subQ0=sQuery(id+"F0.wireOp",EDGE,"E4.3");var subQ1=sQuery(id+"F0.wireOp",EDGE,"E4.2");Q2=makeQuery(id+"F10.boolean.opBoolean","MERGE",EDGE,{"derivedFrom":[makeQuery(id+"F9.opExtrude","SWEPT_EDGE",EDGE,{"disambiguationData":[OSD([subQ1,subQ0])]}),makeQuery(id+"F10.opExtrude","SWEPT_EDGE",EDGE,{"disambiguationData":[OSD([subQ1,subQ0])]})]});}
            var Q3;
            {var subQ0=sQuery(id+"F0.wireOp",EDGE,"E4.3");var subQ1=sQuery(id+"F0.wireOp",EDGE,"E4.0");Q3=makeQuery(id+"F10.boolean.opBoolean","MERGE",EDGE,{"derivedFrom":[makeQuery(id+"F9.opExtrude","SWEPT_EDGE",EDGE,{"disambiguationData":[OSD([subQ1,subQ0])]}),makeQuery(id+"F10.opExtrude","SWEPT_EDGE",EDGE,{"disambiguationData":[OSD([subQ1,subQ0])]})]});}
            fillet(context, id + "F36", {"entities" : qUnion([Q0, Q1, Q2, Q3]), "radius" : 10 * mm, "tangentPropagation" : true, "allowEdgeOverflow" : false});
        }
        {
            var Q0;
            {var subQ0=sQuery(id+"F26.wireOp",EDGE,"E32.bottom");var subQ1=sQuery(id+"F11.wireOp",EDGE,"E10.right");var subQ2=makeQuery(id+"F27.opExtrude","SWEPT_FACE",FACE,{"disambiguationData":[OSD([subQ0])]});Q0=makeQuery(id+"F34.boolean.opBoolean","MERGE",FACE,{"derivedFrom":[makeQuery(id+"F30.boolean.opBoolean","MERGE",FACE,{"derivedFrom":[makeQuery(id+"F12.opExtrude","CAP_FACE",FACE,{"disambiguationData":[OSD([sQuery(id+"F11.wireOp",EDGE,"E10.bottom"),sQuery(id+"F11.wireOp",EDGE,"E10.top"),sQuery(id+"F11.wireOp",EDGE,"E10.left"),subQ1])],"isStart":false}),makeQuery(id+"F30.opPattern","COPY",FACE,{"derivedFrom":makeQuery(id+"F29.opPattern","COPY",FACE,{"derivedFrom":subQ2,"instanceName":"1"}),"instanceName":"1"})]}),makeQuery(id+"F30.boolean.opBoolean","MERGE",FACE,{"derivedFrom":[makeQuery(id+"F12.opExtrude","CAP_FACE",FACE,{"disambiguationData":[OSD([sQuery(id+"F11.wireOp",EDGE,"E11.MirrorCS"),sQuery(id+"F11.wireOp",EDGE,"E12.MirrorCS"),sQuery(id+"F11.wireOp",EDGE,"E13.MirrorCS"),sQuery(id+"F11.wireOp",EDGE,"E14.MirrorCS")])],"isStart":false}),makeQuery(id+"F30.opPattern","COPY",FACE,{"derivedFrom":subQ2,"instanceName":"1"})]}),makeQuery(id+"F34.opExtrude","SWEPT_FACE",FACE,{"disambiguationData":[OSD([subQ1,subQ0,sQuery(id+"F26.wireOp",EDGE,"E32.right")])]})]});}
            extrude(context, id + "F37", {"entities" : qUnion([Q0]), "operationType" : NewBodyOperationType.REMOVE, "oppositeDirection" : true, "depth" : 0.2 * mm, "offsetDistance" : 25 * mm});
        }
        {
            var Q0;
            Q0=makeQuery(id+"F17.opPattern","COPY",FACE,{"derivedFrom":makeQuery(id+"F16.opExtrude","CAP_FACE",FACE,{"disambiguationData":[OSD([sQuery(id+"F15.wireOp",EDGE,"E20.bottom"),sQuery(id+"F15.wireOp",EDGE,"E20.top"),sQuery(id+"F15.wireOp",EDGE,"E20.left"),sQuery(id+"F15.wireOp",EDGE,"E20.right")])],"isStart":false}),"instanceName":"1"});
            extrude(context, id + "F38", {"entities" : qUnion([Q0]), "operationType" : NewBodyOperationType.REMOVE, "oppositeDirection" : true, "depth" : 0.2 * mm, "offsetDistance" : 25 * mm});
        }
        {
            var Q0;
            Q0=makeQuery(id+"F16.opExtrude","CAP_FACE",FACE,{"disambiguationData":[OSD([sQuery(id+"F15.wireOp",EDGE,"E20.bottom"),sQuery(id+"F15.wireOp",EDGE,"E20.top"),sQuery(id+"F15.wireOp",EDGE,"E20.left"),sQuery(id+"F15.wireOp",EDGE,"E20.right")])],"isStart":false});
            extrude(context, id + "F39", {"entities" : qUnion([Q0]), "operationType" : NewBodyOperationType.REMOVE, "oppositeDirection" : true, "depth" : 0.2 * mm, "offsetDistance" : 25 * mm});
        }
        {
            var Q0;
            {var subQ0=sQuery(id+"F26.wireOp",EDGE,"E32.bottom");var subQ1=sQuery(id+"F13.wireOp",EDGE,"E17.MirrorCS");var subQ2=makeQuery(id+"F27.opExtrude","SWEPT_FACE",FACE,{"disambiguationData":[OSD([subQ0])]});Q0=makeQuery(id+"F34.boolean.opBoolean","MERGE",FACE,{"derivedFrom":[makeQuery(id+"F30.boolean.opBoolean","MERGE",FACE,{"derivedFrom":[makeQuery(id+"F14.opExtrude","CAP_FACE",FACE,{"disambiguationData":[OSD([sQuery(id+"F13.wireOp",EDGE,"E15.bottom"),sQuery(id+"F13.wireOp",EDGE,"E15.top"),sQuery(id+"F13.wireOp",EDGE,"E15.left"),sQuery(id+"F13.wireOp",EDGE,"E15.right")])],"isStart":false}),subQ2]}),makeQuery(id+"F30.boolean.opBoolean","MERGE",FACE,{"derivedFrom":[makeQuery(id+"F14.opExtrude","CAP_FACE",FACE,{"disambiguationData":[OSD([sQuery(id+"F13.wireOp",EDGE,"E16.MirrorCS"),subQ1,sQuery(id+"F13.wireOp",EDGE,"E18.MirrorCS"),sQuery(id+"F13.wireOp",EDGE,"E19.MirrorCS")])],"isStart":false}),makeQuery(id+"F29.opPattern","COPY",FACE,{"derivedFrom":subQ2,"instanceName":"1"})]}),makeQuery(id+"F34.opExtrude","SWEPT_FACE",FACE,{"disambiguationData":[OSD([subQ1,subQ0,sQuery(id+"F26.wireOp",EDGE,"E32.right")])]})]});}
            extrude(context, id + "F40", {"entities" : qUnion([Q0]), "operationType" : NewBodyOperationType.REMOVE, "oppositeDirection" : true, "depth" : 0.2 * mm, "offsetDistance" : 25 * mm});
        }
        {
            var Q0;
            Q0=makeQuery(id+"F40.boolean.opBoolean","COPY",FACE,{"derivedFrom":makeQuery(id+"F40.opExtrude","CAP_FACE",FACE,{"disambiguationData":[OSD([sQuery(id+"F13.wireOp",EDGE,"E15.bottom"),sQuery(id+"F13.wireOp",EDGE,"E15.top"),sQuery(id+"F13.wireOp",EDGE,"E15.left"),sQuery(id+"F13.wireOp",EDGE,"E15.right"),sQuery(id+"F13.wireOp",EDGE,"E16.MirrorCS"),sQuery(id+"F13.wireOp",EDGE,"E17.MirrorCS"),sQuery(id+"F13.wireOp",EDGE,"E18.MirrorCS"),sQuery(id+"F13.wireOp",EDGE,"E19.MirrorCS"),sQuery(id+"F26.wireOp",EDGE,"E32.bottom"),sQuery(id+"F26.wireOp",EDGE,"E32.right")])],"isStart":false})});
            var sketch = newSketch(context, id + "F41", { "sketchPlane" : qUnion([Q0])});
            skLineSegment(sketch, "E38.bottom", {"start": v(30, -10) * mm, "end": v(-30, -10) * mm});
            skLineSegment(sketch, "E38.top", {"start": v(30, 0) * mm, "end": v(-30, 0) * mm});
            skLineSegment(sketch, "E38.left", {"start": v(30, -10) * mm, "end": v(30, 0) * mm});
            skLineSegment(sketch, "E38.right", {"start": v(-30, -10) * mm, "end": v(-30, 0) * mm});
            skSolve(sketch);
        }
        {
            var Q0;
            Q0=qSketchRegion(id+"F41",true);
            var Q1;
            {var subQ0=sQuery(id+"F0.wireOp",EDGE,"E3.right");var subQ7=sQuery(id+"F0.wireOp",EDGE,"E3.bottom");Q1=makeQuery(id+"F14.boolean.opBoolean","SPLIT",FACE,{"disambiguationData":[TD([makeQuery(id+"F10.opExtrude","SWEPT_FACE",FACE,{"disambiguationData":[OSD([subQ0])]})])],"derivedFrom":makeQuery(id+"F10.opExtrude","SWEPT_FACE",FACE,{"disambiguationData":[OSD([subQ7])]})});}
            extrude(context, id + "F42", {"entities" : qUnion([Q0]), "operationType" : NewBodyOperationType.REMOVE, "endBound" : BoundingType.UP_TO_SURFACE, "oppositeDirection" : true, "depth" : 25 * mm, "endBoundEntityFace" : qUnion([Q1]), "offsetDistance" : 25 * mm});
        }
        {
            var Q0;
            Q0=makeQuery(id+"F37.boolean.opBoolean","COPY",FACE,{"derivedFrom":makeQuery(id+"F37.opExtrude","CAP_FACE",FACE,{"disambiguationData":[OSD([sQuery(id+"F11.wireOp",EDGE,"E10.bottom"),sQuery(id+"F11.wireOp",EDGE,"E10.top"),sQuery(id+"F11.wireOp",EDGE,"E10.left"),sQuery(id+"F11.wireOp",EDGE,"E10.right"),sQuery(id+"F11.wireOp",EDGE,"E11.MirrorCS"),sQuery(id+"F11.wireOp",EDGE,"E12.MirrorCS"),sQuery(id+"F11.wireOp",EDGE,"E13.MirrorCS"),sQuery(id+"F11.wireOp",EDGE,"E14.MirrorCS"),sQuery(id+"F26.wireOp",EDGE,"E32.bottom"),sQuery(id+"F26.wireOp",EDGE,"E32.right")])],"isStart":false})});
            var sketch = newSketch(context, id + "F43", { "sketchPlane" : qUnion([Q0])});
            skLineSegment(sketch, "E39.bottom", {"start": v(30, -10) * mm, "end": v(-30, -10) * mm});
            skLineSegment(sketch, "E39.top", {"start": v(30, 0) * mm, "end": v(-30, 0) * mm});
            skLineSegment(sketch, "E39.left", {"start": v(30, -10) * mm, "end": v(30, 0) * mm});
            skLineSegment(sketch, "E39.right", {"start": v(-30, -10) * mm, "end": v(-30, 0) * mm});
            skSolve(sketch);
        }
        {
            var Q0;
            Q0=qSketchRegion(id+"F43",true);
            var Q1;
            {var subQ0=sQuery(id+"F0.wireOp",EDGE,"E3.left");var subQ6=sQuery(id+"F0.wireOp",EDGE,"E3.top");Q1=makeQuery(id+"F12.boolean.opBoolean","SPLIT",FACE,{"disambiguationData":[TD([makeQuery(id+"F10.opExtrude","SWEPT_FACE",FACE,{"disambiguationData":[OSD([subQ0])]})])],"derivedFrom":makeQuery(id+"F10.opExtrude","SWEPT_FACE",FACE,{"disambiguationData":[OSD([subQ6])]})});}
            extrude(context, id + "F44", {"entities" : qUnion([Q0]), "operationType" : NewBodyOperationType.REMOVE, "endBound" : BoundingType.UP_TO_SURFACE, "oppositeDirection" : true, "depth" : 25 * mm, "endBoundEntityFace" : qUnion([Q1]), "offsetDistance" : 25 * mm});
        }
        {
            var Q0;
            Q0=makeQuery(id+"F37.boolean.opBoolean","COPY",EDGE,{"derivedFrom":makeQuery(id+"F37.opExtrude","CAP_EDGE",EDGE,{"disambiguationData":[OSD([sQuery(id+"F11.wireOp",EDGE,"E11.MirrorCS"),sQuery(id+"F26.wireOp",EDGE,"E32.bottom"),sQuery(id+"F26.wireOp",EDGE,"E32.left")])],"isStart":false})});
            var Q1;
            Q1=makeQuery(id+"F44.boolean.opBoolean","COPY",EDGE,{"derivedFrom":makeQuery(id+"F44.opExtrude","CAP_EDGE",EDGE,{"disambiguationData":[OSD([sQuery(id+"F43.wireOp",EDGE,"E39.left")])],"isStart":true})});
            var Q2;
            Q2=makeQuery(id+"F44.boolean.opBoolean","COPY",EDGE,{"derivedFrom":makeQuery(id+"F44.opExtrude","CAP_EDGE",EDGE,{"disambiguationData":[OSD([sQuery(id+"F43.wireOp",EDGE,"E39.right")])],"isStart":true})});
            var Q3;
            Q3=makeQuery(id+"F37.boolean.opBoolean","COPY",EDGE,{"derivedFrom":makeQuery(id+"F37.opExtrude","CAP_EDGE",EDGE,{"disambiguationData":[OSD([sQuery(id+"F11.wireOp",EDGE,"E10.left"),sQuery(id+"F26.wireOp",EDGE,"E32.bottom"),sQuery(id+"F26.wireOp",EDGE,"E32.left")])],"isStart":false})});
            var Q4;
            Q4=makeQuery(id+"F42.boolean.opBoolean","COPY",EDGE,{"derivedFrom":makeQuery(id+"F42.opExtrude","CAP_EDGE",EDGE,{"disambiguationData":[OSD([sQuery(id+"F41.wireOp",EDGE,"E38.right")])],"isStart":true})});
            var Q5;
            Q5=makeQuery(id+"F40.boolean.opBoolean","COPY",EDGE,{"derivedFrom":makeQuery(id+"F40.opExtrude","CAP_EDGE",EDGE,{"disambiguationData":[OSD([sQuery(id+"F13.wireOp",EDGE,"E15.left"),sQuery(id+"F26.wireOp",EDGE,"E32.bottom"),sQuery(id+"F26.wireOp",EDGE,"E32.left")])],"isStart":false})});
            var Q6;
            Q6=makeQuery(id+"F42.boolean.opBoolean","COPY",EDGE,{"derivedFrom":makeQuery(id+"F42.opExtrude","CAP_EDGE",EDGE,{"disambiguationData":[OSD([sQuery(id+"F41.wireOp",EDGE,"E38.left")])],"isStart":true})});
            var Q7;
            Q7=makeQuery(id+"F40.boolean.opBoolean","COPY",EDGE,{"derivedFrom":makeQuery(id+"F40.opExtrude","CAP_EDGE",EDGE,{"disambiguationData":[OSD([sQuery(id+"F13.wireOp",EDGE,"E16.MirrorCS"),sQuery(id+"F26.wireOp",EDGE,"E32.bottom"),sQuery(id+"F26.wireOp",EDGE,"E32.left")])],"isStart":false})});
            fillet(context, id + "F45", {"entities" : qUnion([Q0, Q1, Q2, Q3, Q4, Q5, Q6, Q7]), "radius" : 5 * mm, "tangentPropagation" : true, "allowEdgeOverflow" : false});
        }
        {
            var Q0;
            Q0=makeQuery(id+"F9.opExtrude","CAP_EDGE",EDGE,{"disambiguationData":[OSD([sQuery(id+"F0.wireOp",EDGE,"E4.1")])],"isStart":false});
            fillet(context, id + "F46", {"entities" : qUnion([Q0]), "radius" : 5 * mm, "tangentPropagation" : true, "allowEdgeOverflow" : false});
        }
    });
